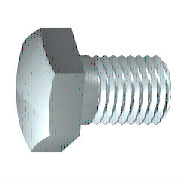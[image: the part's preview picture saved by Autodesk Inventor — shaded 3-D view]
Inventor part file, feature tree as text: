
AUTODESK INVENTOR PART (.ipt)
format: ipt  version: 2020 (Build 240168000, 168)  size: 192,512 bytes
history: native  units: mm (DEFAULTED — no unit token found)
features: sketch x3, extrude x1, chamfer x1, plane x1
ambient origin geometry x7: Origin, YZ Plane, XZ Plane, X Axis, Y Axis, Z Axis, Center Point
bodies: Solid1 (feature_tree), Body (feature_tree)
feature tree (6):
  extrude  "Head"  Depth=47.9mm
  chamfer  "Chamfer1"  Distance=2.4mm
  plane  "Work Plane1"
  sketch  "Sketch1"  dims[d0=50.0mm d1=47.9mm]
  sketch  "Sketch2"  dims[d2=4.0mm]
  sketch  "Sketch4"  dims[d12=90.0deg d3=2.4mm d4=0.0mm d5=30.0deg d21=90.0deg d6=0.429415mm d7=0.429515mm d8=0.0mm d9=0.4001mm d10=5.9mm d11=7.0mm d13=0.429515mm d14=3.621114mm d15=47.9mm d16=0.0mm d19=7.0mm d55=45.0deg d57=0.0mm d58=0.0mm]
